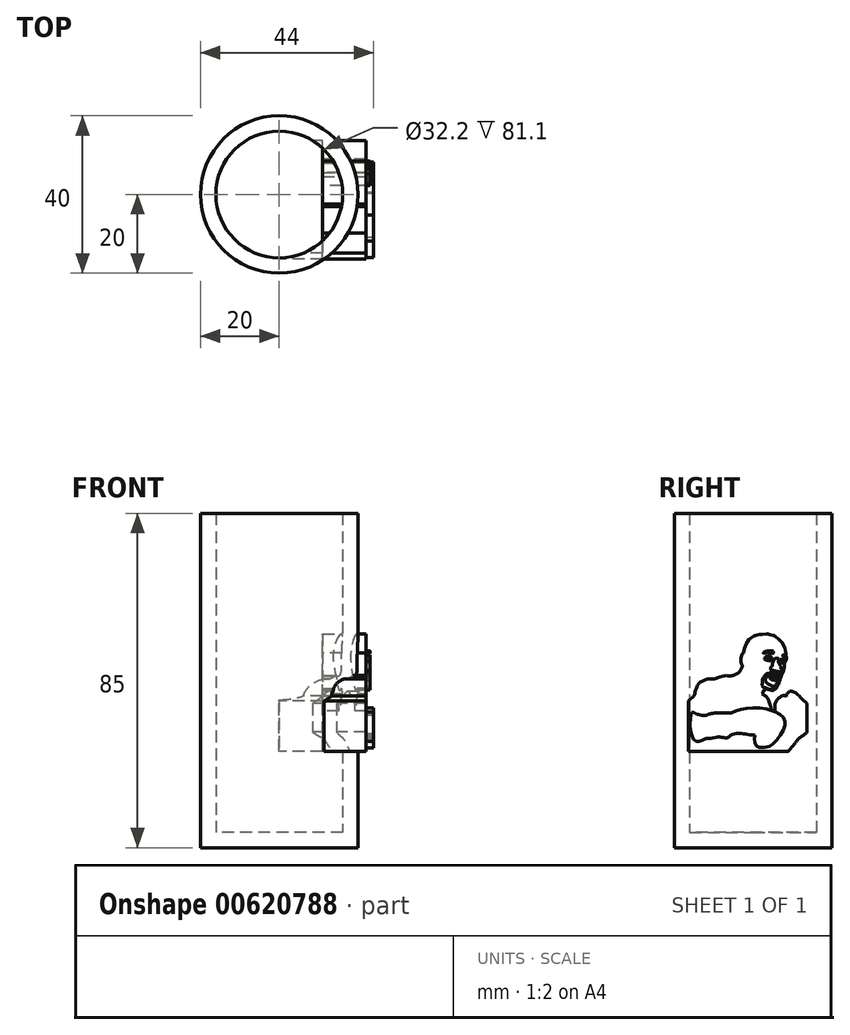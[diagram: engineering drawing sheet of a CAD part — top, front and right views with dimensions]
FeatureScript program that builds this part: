
annotation { "Feature Type Name" : "Feature", "Feature Type Description" : "" }
export const myFeature = defineFeature(function(context is Context, id is Id, definition is map)
    precondition{}
    {
        {
            var Q0;
            Q0=qCreatedBy(makeId("Top.planeOp"),FACE);
            var sketch = newSketch(context, id + "F0", { "sketchPlane" : qUnion([Q0])});
            skCircle(sketch, "E0", {"center": v(0, 0) * mm, "radius": 20 * mm});
            skSolve(sketch);
        }
        {
            var Q0;
            Q0 = qSketchRegion(id + "F0", true);
            extrude(context, id + "F1", {"entities" : qUnion([Q0]), "depth" : 85 * mm, "offsetDistance" : 25.4 * mm});
        }
        {
            var Q0;
            Q0=makeQuery(id+"F1.opExtrude","CAP_FACE",FACE,{"disambiguationData":[OSD([sQuery(id+"F0.wireOp",EDGE,"E0")])],"isStart":false});
            shell(context, id + "F2", {"entities" : qUnion([Q0]), "thickness" : 3.9 * mm});
        }
        {
            var Q0;
            Q0=qCreatedBy(makeId("Right.planeOp"),FACE);
            var sketch = newSketch(context, id + "F3", { "sketchPlane" : qUnion([Q0])});
            skFitSpline(sketch, "E1", {"points": [v(-16.45, 37.32) * mm, v(-14.95, 38.53) * mm], "startDerivative": vector(1.5, 1.2) * mm, "endDerivative": vector(1.5, 1.2) * mm});
            skFitSpline(sketch, "E2", {"points": [v(-14.95, 38.53) * mm, v(-14.69, 39.68) * mm, v(-14.38, 40.61) * mm, v(-13.68, 41.78) * mm, v(-12.74, 42.43) * mm, v(-12.01, 42.74) * mm, v(-11.08, 42.92) * mm, v(-10.33, 42.95) * mm, v(-9.87, 42.9) * mm], "startDerivative": vector(1.8, 8.5) * mm, "endDerivative": vector(4.86, -0.8) * mm});
            skFitSpline(sketch, "E3", {"points": [v(-9.87, 42.9) * mm, v(-9.14, 43.13) * mm, v(-7.93, 43.57) * mm, v(-6.83, 43.73) * mm, v(-5.52, 43.7) * mm, v(-4.38, 44.05) * mm, v(-3.52, 44.58) * mm, v(-3.1, 45.26) * mm, v(-2.73, 46.3) * mm, v(-3.07, 47) * mm, v(-3.07, 48.07) * mm, v(-2.97, 48.7) * mm, v(-2.44, 49.5) * mm], "startDerivative": vector(9.29, 2.82) * mm, "endDerivative": vector(7.98, 10.03) * mm});
            skFitSpline(sketch, "E4", {"points": [v(-2.44, 49.5) * mm, v(-2.25, 50.33) * mm, v(-1.9, 51.46) * mm, v(-1.46, 52.3) * mm, v(-0.72, 53.17) * mm, v(0.84, 54.04) * mm, v(2.12, 54.23) * mm, v(4.44, 54.22) * mm, v(5.71, 53.7) * mm, v(6.84, 52.78) * mm, v(7.75, 51.52) * mm, v(8.32, 50.1) * mm, v(8.46, 48.56) * mm, v(8.4, 47.47) * mm, v(8.04, 46.93) * mm, v(7.93, 46.53) * mm, v(7.96, 46.1) * mm, v(7.8, 45.24) * mm, v(7.44, 44.23) * mm, v(7.12, 43.44) * mm, v(6.85, 42.68) * mm, v(6.53, 41.63) * mm, v(6.26, 41.36) * mm, v(6.07, 40.84) * mm, v(5.49, 40.16) * mm, v(4.7, 39.99) * mm, v(4, 40.17) * mm, v(3.13, 40.4) * mm, v(2.3, 39.14) * mm], "startDerivative": vector(5.46, 24.06) * mm, "endDerivative": vector(-17.03, -40.02) * mm});
            skFitSpline(sketch, "E5", {"points": [v(2.3, 39.14) * mm, v(3, 38.7) * mm, v(3.65, 38.1) * mm, v(4, 37.39) * mm, v(4.36, 36.26) * mm, v(4.54, 35.67) * mm, v(4.57, 35.13) * mm, v(5.53, 34.74) * mm], "startDerivative": vector(4.94, -2.92) * mm, "endDerivative": vector(7.89, -1.72) * mm});
            skFitSpline(sketch, "E6", {"points": [v(5.53, 34.74) * mm, v(5.53, 35.76) * mm, v(5.7, 36.88) * mm, v(6.2, 37.73) * mm, v(6.98, 38.38) * mm, v(7.7, 38.72) * mm, v(8.5, 38.43) * mm], "startDerivative": vector(-0.13, 5.81) * mm, "endDerivative": vector(5.2, -2.86) * mm});
            skFitSpline(sketch, "E7", {"points": [v(8.5, 38.43) * mm, v(8.58, 38.96) * mm, v(8.99, 39.42) * mm, v(9.41, 39.77) * mm, v(9.93, 39.75) * mm, v(10.52, 39.57) * mm, v(11.37, 38.9) * mm, v(13.68, 36.67) * mm], "startDerivative": vector(0.03, 5) * mm, "endDerivative": vector(9.5, -9.33) * mm});
            skLineSegment(sketch, "E8", {"start": v(13.68, 36.67) * mm, "end": v(13.68, 29.38) * mm});
            skFitSpline(sketch, "E9", {"points": [v(13.68, 29.38) * mm, v(12.94, 28.66) * mm, v(11.46, 27.61) * mm, v(10.79, 26.73) * mm, v(9, 24.5) * mm], "startDerivative": vector(-3.12, -3.52) * mm, "endDerivative": vector(-6.33, -7.55) * mm});
            skLineSegment(sketch, "E10", {"start": v(9, 24.5) * mm, "end": v(-16.45, 24.5) * mm});
            skLineSegment(sketch, "E11", {"start": v(-16.45, 24.5) * mm, "end": v(-16.45, 37.32) * mm});
            skSolve(sketch);
        }
        {
            var Q0;
            Q0=qCreatedBy(makeId("Right.planeOp"),FACE);
            var sketch = newSketch(context, id + "F4", { "sketchPlane" : qUnion([Q0])});
            skFitSpline(sketch, "E12", {"points": [v(-11.8, 33.63) * mm, v(-11.43, 33.85) * mm, v(-10.57, 34.13) * mm, v(-8.78, 34.3) * mm, v(-7.48, 34.3) * mm, v(-6.41, 34.26) * mm, v(-5.2, 34.35) * mm], "startDerivative": vector(3.1, 2.14) * mm, "endDerivative": vector(6.94, 0.7) * mm});
            skFitSpline(sketch, "E13", {"points": [v(-5.2, 34.35) * mm, v(-4.57, 34.75) * mm, v(-3.23, 35.15) * mm, v(-1.55, 35.4) * mm, v(0.72, 35.52) * mm, v(3.21, 35.34) * mm, v(4.48, 34.97) * mm, v(5.67, 34.52) * mm, v(6.85, 33.87) * mm, v(7.66, 33.14) * mm, v(8.05, 32.25) * mm, v(8.17, 31.36) * mm, v(7.88, 30.26) * mm, v(7.02, 28.74) * mm, v(5.84, 27.16) * mm, v(4.8, 26.08) * mm, v(3.88, 25.72) * mm, v(2.51, 25.43) * mm, v(1.33, 25.64) * mm, v(0.84, 25.93) * mm, v(0.58, 26.43) * mm, v(0.42, 27.06) * mm, v(0.43, 27.87) * mm, v(0.43, 28.52) * mm], "startDerivative": vector(16.46, 12.13) * mm, "endDerivative": vector(-0.41, 19.55) * mm});
            skFitSpline(sketch, "E14", {"points": [v(0.43, 28.52) * mm, v(0.08, 28.62) * mm, v(-0.4, 28.63) * mm, v(-1.63, 28.84) * mm, v(-2.3, 28.98) * mm, v(-3.3, 29.02) * mm, v(-4.32, 29.01) * mm, v(-5.2, 28.8) * mm, v(-6.06, 28.3) * mm, v(-6.8, 27.9) * mm, v(-7.5, 27.97) * mm, v(-8.09, 28.12) * mm, v(-8.76, 28.15) * mm, v(-9.78, 27.99) * mm, v(-10.8, 27.83) * mm, v(-10.96, 27.83) * mm], "startDerivative": vector(-7.47, 2.88) * mm, "endDerivative": vector(-3.97, 0.3) * mm});
            skFitSpline(sketch, "E15", {"points": [v(-11.8, 33.63) * mm, v(-12.47, 33.63) * mm, v(-13.68, 33.82) * mm, v(-14.46, 34.05) * mm, v(-15.5, 34.4) * mm, v(-14.9, 27.37) * mm, v(-12.46, 27.53) * mm, v(-11.96, 27.73) * mm, v(-10.96, 27.83) * mm], "startDerivative": vector(-7.34, -0.45) * mm, "endDerivative": vector(11.22, 0.78) * mm});
            skSolve(sketch);
        }
        {
            var Q0;
            Q0 = qSketchRegion(id + "F3", true);
            extrude(context, id + "F5", {"entities" : qUnion([Q0]), "operationType" : NewBodyOperationType.ADD, "depth" : 22 * mm, "offsetDistance" : 25 * mm});
        }
        {
            var Q0;
            Q0 = qSketchRegion(id + "F4", true);
            extrude(context, id + "F6", {"entities" : qUnion([Q0]), "operationType" : NewBodyOperationType.ADD, "depth" : 24 * mm, "offsetDistance" : 25 * mm});
        }
        {
            var Q0;
            Q0=qCreatedBy(makeId("Right.planeOp"),FACE);
            var sketch = newSketch(context, id + "F7", { "sketchPlane" : qUnion([Q0])});
            skFitSpline(sketch, "E16", {"points": [v(4.95, 44.59) * mm, v(4.22, 44.42) * mm, v(3.59, 44.3) * mm, v(3.15, 43.96) * mm, v(2.73, 43.37) * mm, v(2.38, 42.87) * mm, v(2.33, 41.97) * mm, v(2.32, 41.35) * mm, v(2.32, 41.02) * mm, v(3.05, 40.64) * mm, v(3.68, 40.44) * mm, v(4.48, 40.23) * mm, v(5.06, 40.17) * mm, v(5.53, 40.33) * mm, v(5.76, 40.6) * mm, v(6, 41.09) * mm, v(6.15, 41.47) * mm, v(6.44, 41.88) * mm, v(6.6, 42.24) * mm, v(6.68, 42.5) * mm, v(6.79, 42.8) * mm, v(6.92, 43.36) * mm, v(6.97, 43.71) * mm, v(6.72, 44.2) * mm, v(6.38, 44.42) * mm, v(5.66, 44.57) * mm, v(4.95, 44.59) * mm]});
            skFitSpline(sketch, "E17", {"points": [v(3.6, 43.62) * mm, v(3.23, 43.21) * mm, v(3.14, 42.77) * mm, v(3.2, 42.3) * mm, v(3.53, 41.88) * mm, v(4.19, 41.48) * mm, v(4.77, 41.17) * mm, v(5.4, 41.03) * mm, v(5.7, 41.2) * mm, v(5.93, 41.61) * mm, v(6.27, 42) * mm, v(6.41, 42.32) * mm, v(6.7, 43.05) * mm, v(6.77, 43.48) * mm, v(6.68, 43.95) * mm, v(6.18, 44.1) * mm, v(5.85, 44.21) * mm, v(5.3, 44.17) * mm, v(4.73, 44.07) * mm, v(4.18, 43.89) * mm, v(3.92, 43.77) * mm, v(3.6, 43.62) * mm]});
            skSolve(sketch);
        }
        {
            var Q0;
            Q0 = qSketchRegion(id + "F7", true);
            extrude(context, id + "F8", {"entities" : qUnion([Q0]), "operationType" : NewBodyOperationType.ADD, "depth" : 23 * mm, "offsetDistance" : 25 * mm});
        }
        {
            var Q0;
            Q0=qCreatedBy(makeId("Right.planeOp"),FACE);
            var sketch = newSketch(context, id + "F9", { "sketchPlane" : qUnion([Q0])});
            skFitSpline(sketch, "E18", {"points": [v(4.14, 43.38) * mm, v(4.58, 42.9) * mm, v(5.13, 42.65) * mm, v(5.83, 42.54) * mm, v(6.18, 42.56) * mm, v(6.41, 42.59) * mm, v(6.5, 42.81) * mm, v(6.26, 43.04) * mm, v(5.98, 43.06) * mm, v(5.57, 43.17) * mm, v(4.9, 43.38) * mm, v(4.5, 43.42) * mm, v(4.14, 43.38) * mm]});
            skFitSpline(sketch, "E19", {"points": [v(4.3, 43.6) * mm, v(4.74, 43.86) * mm, v(5.21, 44.03) * mm, v(5.57, 44.09) * mm, v(5.79, 44.09) * mm, v(6.03, 44) * mm, v(6.14, 43.93) * mm, v(6.17, 43.88) * mm, v(6.34, 43.88) * mm, v(6.57, 43.87) * mm, v(6.7, 43.78) * mm, v(6.73, 43.6) * mm, v(6.7, 43.34) * mm, v(6.65, 43.22) * mm, v(6.46, 43.13) * mm, v(6.07, 43.17) * mm, v(5.74, 43.24) * mm, v(5.67, 43.28) * mm, v(5.49, 43.32) * mm, v(5.12, 43.43) * mm, v(4.65, 43.52) * mm, v(4.3, 43.6) * mm]});
            skSolve(sketch);
        }
        {
            var Q0;
            Q0 = qSketchRegion(id + "F9", true);
            extrude(context, id + "F10", {"entities" : qUnion([Q0]), "operationType" : NewBodyOperationType.ADD, "depth" : 23 * mm, "offsetDistance" : 25 * mm});
        }
        {
            var Q0;
            Q0=qCreatedBy(makeId("Right.planeOp"),FACE);
            var sketch = newSketch(context, id + "F11", { "sketchPlane" : qUnion([Q0])});
            skFitSpline(sketch, "E20", {"points": [v(2.88, 48.13) * mm, v(3.4, 48.6) * mm, v(3.89, 48.88) * mm, v(4.28, 48.84) * mm, v(4.57, 48.5) * mm, v(4.9, 47.87) * mm, v(4.43, 47.54) * mm, v(3.53, 47.64) * mm, v(3.06, 47.87) * mm, v(2.88, 48.13) * mm]});
            skFitSpline(sketch, "E21", {"points": [v(6.63, 47.61) * mm, v(7, 47.85) * mm, v(7.32, 47.91) * mm, v(7.58, 47.78) * mm, v(7.73, 47.4) * mm, v(7.7, 47) * mm, v(7.37, 46.99) * mm, v(6.86, 47.2) * mm, v(6.63, 47.61) * mm]});
            skFitSpline(sketch, "E22", {"points": [v(3.58, 48.37) * mm, v(3.36, 48.2) * mm, v(3.37, 48.02) * mm, v(3.82, 47.92) * mm, v(4.3, 47.87) * mm, v(4.54, 47.91) * mm, v(4.6, 48.08) * mm, v(4.44, 48.33) * mm], "startDerivative": vector(-1.99, -0.97) * mm, "endDerivative": vector(-1.43, 1.74) * mm});
            skFitSpline(sketch, "E23", {"points": [v(4.44, 48.33) * mm, v(4.34, 48.13) * mm, v(4.2, 48) * mm, v(4.05, 48) * mm, v(3.9, 48.08) * mm, v(3.8, 48.19) * mm, v(3.78, 48.3) * mm, v(3.78, 48.39) * mm, v(3.58, 48.37) * mm], "startDerivative": vector(-0.63, -1.38) * mm, "endDerivative": vector(-1.85, -0.44) * mm});
            skFitSpline(sketch, "E24", {"points": [v(6.86, 47.58) * mm, v(6.88, 47.43) * mm, v(6.96, 47.3) * mm, v(7.14, 47.2) * mm, v(7.36, 47.33) * mm, v(7.38, 47.4) * mm], "startDerivative": vector(-0.01, -0.81) * mm, "endDerivative": vector(0.02, 0.49) * mm});
            skFitSpline(sketch, "E25", {"points": [v(7.38, 47.4) * mm, v(7.48, 47.33) * mm, v(7.41, 47.2) * mm, v(7.27, 47.12) * mm, v(7.03, 47.15) * mm, v(6.9, 47.24) * mm, v(6.8, 47.38) * mm, v(6.77, 47.48) * mm, v(6.77, 47.53) * mm, v(6.86, 47.58) * mm], "startDerivative": vector(1.28, -0.59) * mm, "endDerivative": vector(1.27, 0.44) * mm});
            skSolve(sketch);
        }
        {
            var Q0;
            Q0 = qSketchRegion(id + "F11", true);
            extrude(context, id + "F12", {"entities" : qUnion([Q0]), "operationType" : NewBodyOperationType.ADD, "depth" : 23 * mm, "offsetDistance" : 25 * mm});
        }
        {
            var Q0;
            Q0=qCreatedBy(makeId("Right.planeOp"),FACE);
            var sketch = newSketch(context, id + "F13", { "sketchPlane" : qUnion([Q0])});
            skFitSpline(sketch, "E26", {"points": [v(3.67, 49.97) * mm, v(2.9, 49.81) * mm, v(2.6, 49.49) * mm, v(3.54, 49.61) * mm, v(4.2, 49.61) * mm, v(4.75, 49.47) * mm, v(5.15, 49.4) * mm, v(5.22, 49.81) * mm, v(4.77, 50.03) * mm, v(3.67, 49.97) * mm]});
            skFitSpline(sketch, "E27", {"points": [v(7.68, 49.01) * mm, v(8.28, 48.76) * mm, v(8.4, 48.33) * mm, v(8.4, 47.81) * mm, v(8.22, 48.15) * mm, v(7.96, 48.46) * mm, v(7.6, 48.63) * mm, v(7.68, 49.01) * mm]});
            skFitSpline(sketch, "E28", {"points": [v(5.63, 48.12) * mm, v(5.14, 47.42) * mm, v(4.92, 46.64) * mm, v(4.96, 46.22) * mm, v(4.58, 45.9) * mm, v(4.6, 45.15) * mm, v(5.4, 45.02) * mm, v(5.99, 44.87) * mm, v(6.3, 44.8) * mm, v(6.4, 44.83) * mm, v(6.65, 44.69) * mm, v(6.8, 44.59) * mm, v(7.05, 44.83) * mm, v(7.3, 45.12) * mm, v(7.17, 45.36) * mm, v(6.99, 46.2) * mm, v(6.7, 46.66) * mm, v(6.43, 47.52) * mm, v(6.45, 48.08) * mm, v(5.63, 48.12) * mm]});
            skSolve(sketch);
        }
        {
            var Q0;
            Q0 = qSketchRegion(id + "F13", true);
            extrude(context, id + "F14", {"entities" : qUnion([Q0]), "operationType" : NewBodyOperationType.ADD, "depth" : 23 * mm, "offsetDistance" : 25 * mm});
        }
        {
            var Q0;
            Q0 = qSketchRegion(id + "F13", true);
            var Q1;
            Q1 = qSketchRegion(id + "F11", true);
            var Q2;
            Q2 = qSketchRegion(id + "F9", true);
            var Q3;
            Q3 = qSketchRegion(id + "F7", true);
            var Q4;
            Q4 = qSketchRegion(id + "F4", true);
            var Q5;
            Q5 = qSketchRegion(id + "F3", true);
            extrude(context, id + "F15", {"entities" : qUnion([Q0, Q1, Q2, Q3, Q4, Q5]), "operationType" : NewBodyOperationType.REMOVE, "depth" : 11 * mm, "offsetDistance" : 25 * mm});
        }
    });
